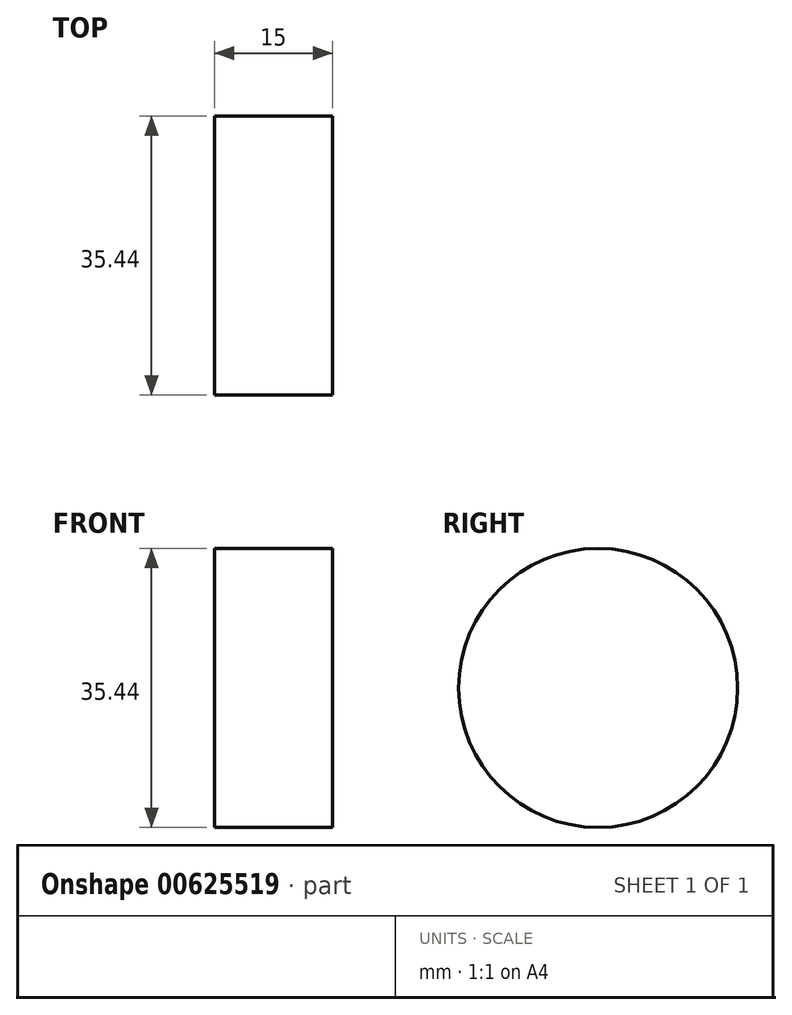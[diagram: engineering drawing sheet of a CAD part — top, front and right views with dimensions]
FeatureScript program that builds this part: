
annotation { "Feature Type Name" : "Feature", "Feature Type Description" : "" }
export const myFeature = defineFeature(function(context is Context, id is Id, definition is map)
    precondition{}
    {
        {
            var Q0;
            Q0=qCreatedBy(makeId("Right.planeOp"),FACE);
            var sketch = newSketch(context, id + "F0", { "sketchPlane" : qUnion([Q0])});
            skCircle(sketch, "E0", {"center": v(0, 0) * mm, "radius": 17.72 * mm});
            skSolve(sketch);
        }
        {
            var Q0;
            Q0 = qSketchRegion(id + "F0", true);
            extrude(context, id + "F1", {"entities" : qUnion([Q0]), "depth" : 15 * mm, "offsetDistance" : 25 * mm});
        }
    });
